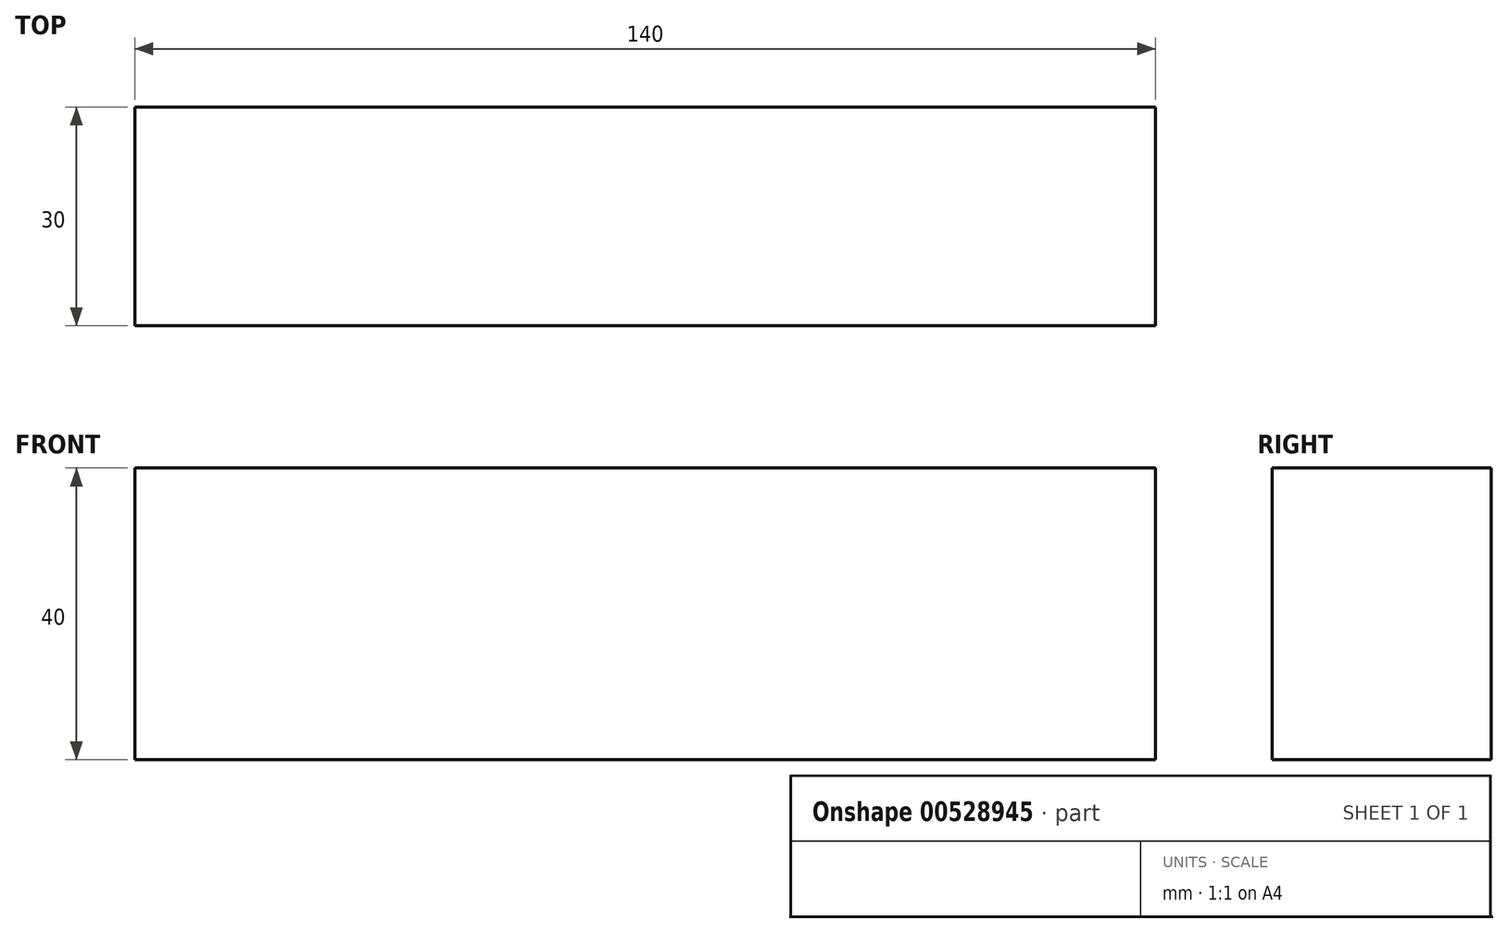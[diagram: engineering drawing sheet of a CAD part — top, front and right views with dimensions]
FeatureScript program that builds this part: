
annotation { "Feature Type Name" : "Feature", "Feature Type Description" : "" }
export const myFeature = defineFeature(function(context is Context, id is Id, definition is map)
    precondition{}
    {
        {
            var Q0;
            Q0=qCreatedBy(makeId("Top.planeOp"),FACE);
            var sketch = newSketch(context, id + "F0", { "sketchPlane" : qUnion([Q0])});
            skLineSegment(sketch, "E0.bottom", {"start": v(70, -15) * mm, "end": v(-70, -15) * mm});
            skLineSegment(sketch, "E0.top", {"start": v(70, 15) * mm, "end": v(-70, 15) * mm});
            skLineSegment(sketch, "E0.left", {"start": v(70, -15) * mm, "end": v(70, 15) * mm});
            skLineSegment(sketch, "E0.right", {"start": v(-70, -15) * mm, "end": v(-70, 15) * mm});
            skPoint(sketch, "E0.middle", {"position": v(0, 0) * mm});
            skSolve(sketch);
        }
        {
            var Q0;
            Q0 = qSketchRegion(id + "F0", true);
            extrude(context, id + "F1", {"entities" : qUnion([Q0]), "depth" : 40 * mm, "offsetDistance" : 25 * mm});
        }
    });
